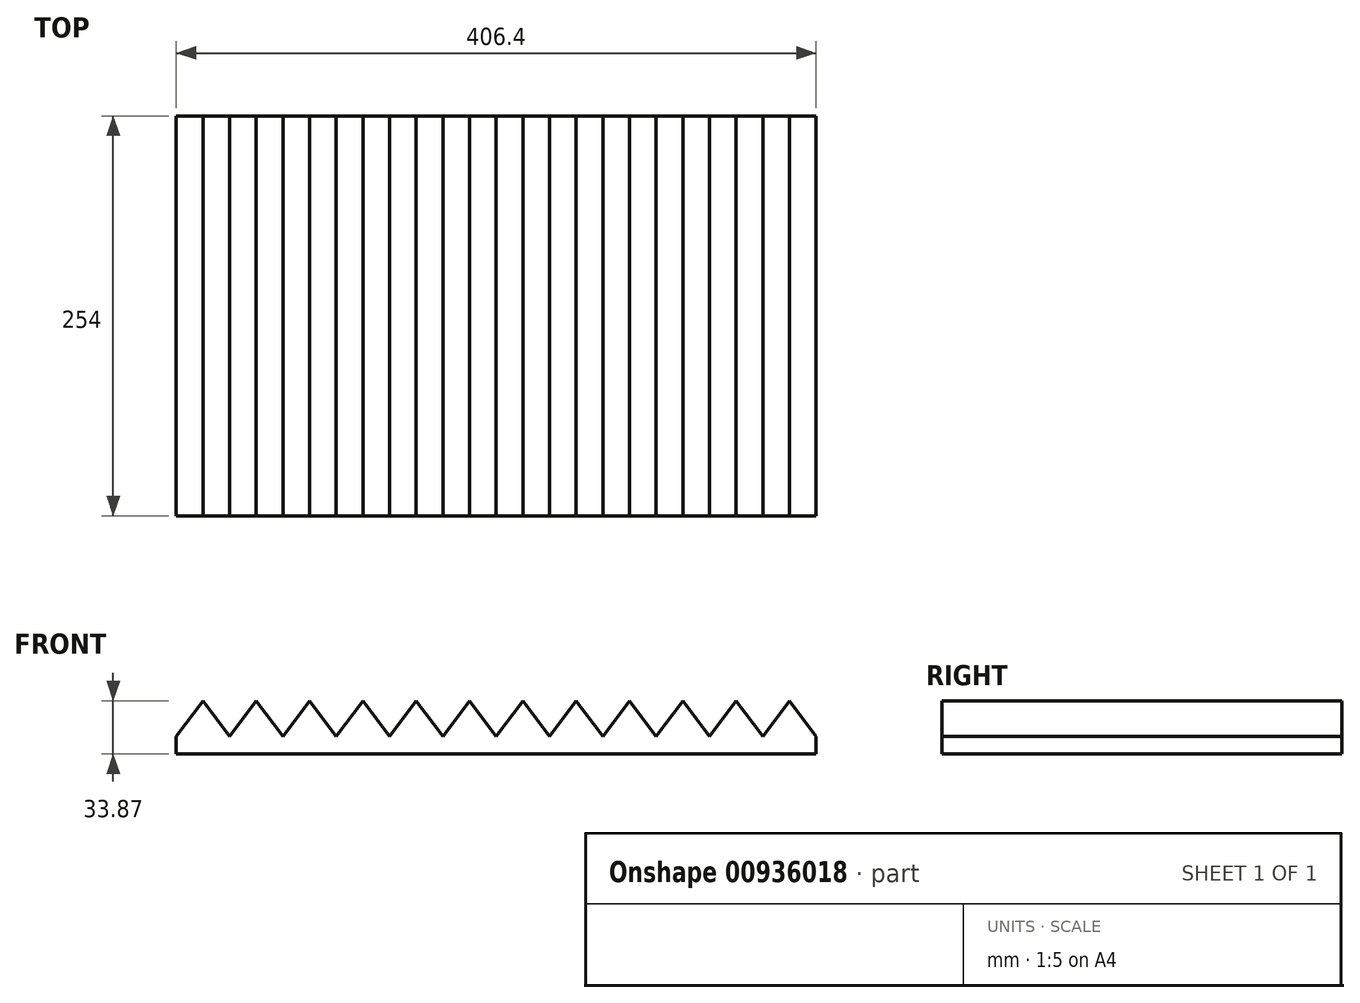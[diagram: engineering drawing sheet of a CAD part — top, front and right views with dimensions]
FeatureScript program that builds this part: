
annotation { "Feature Type Name" : "Feature", "Feature Type Description" : "" }
export const myFeature = defineFeature(function(context is Context, id is Id, definition is map)
    precondition{}
    {
        {
            var Q0;
            Q0=qCreatedBy(makeId("Front.planeOp"),FACE);
            var sketch = newSketch(context, id + "F0", { "sketchPlane" : qUnion([Q0])});
            skLineSegment(sketch, "E0.bottom", {"start": v(-198.97, -4.94) * mm, "end": v(207.43, -4.94) * mm});
            skLineSegment(sketch, "E0.top", {"start": v(-198.97, 6.35) * mm, "end": v(207.43, 6.35) * mm});
            skLineSegment(sketch, "E0.left", {"start": v(-198.97, -4.94) * mm, "end": v(-198.97, 6.35) * mm});
            skLineSegment(sketch, "E0.right", {"start": v(207.43, -4.94) * mm, "end": v(207.43, 6.35) * mm});
            skLineSegment(sketch, "E1", {"start": v(-198.97, 6.35) * mm, "end": v(-165.1, 6.35) * mm});
            skPoint(sketch, "E2", {"position": v(-198.97, 6.35) * mm});
            skLineSegment(sketch, "E3", {"start": v(-165.1, 6.35) * mm, "end": v(-198.97, 6.35) * mm});
            skLineSegment(sketch, "E4", {"start": v(-182.03, 6.35) * mm, "end": v(-182.03, 28.93) * mm});
            skLineSegment(sketch, "E5", {"start": v(-165.1, 6.35) * mm, "end": v(-182.03, 28.93) * mm});
            skLineSegment(sketch, "E6", {"start": v(-198.97, 6.35) * mm, "end": v(-182.03, 28.93) * mm});
            skLineSegment(sketch, "E7.direction1", {"start": v(-198.97, 6.35) * mm, "end": v(-129.54, 6.35) * mm, "construction": true});
            skLineSegment(sketch, "E8.1.0.0", {"start": v(-165.1, 6.35) * mm, "end": v(-148.17, 28.93) * mm});
            skLineSegment(sketch, "E8.1.0.1", {"start": v(-148.17, 6.35) * mm, "end": v(-148.17, 28.93) * mm});
            skLineSegment(sketch, "E8.1.0.2", {"start": v(-131.23, 6.35) * mm, "end": v(-148.17, 28.93) * mm});
            skLineSegment(sketch, "E8.2.0.0", {"start": v(-131.23, 6.35) * mm, "end": v(-114.3, 28.93) * mm});
            skLineSegment(sketch, "E8.2.0.1", {"start": v(-114.3, 6.35) * mm, "end": v(-114.3, 28.93) * mm});
            skLineSegment(sketch, "E8.2.0.2", {"start": v(-97.37, 6.35) * mm, "end": v(-114.3, 28.93) * mm});
            skLineSegment(sketch, "E8.3.0.0", {"start": v(-97.37, 6.35) * mm, "end": v(-80.43, 28.93) * mm});
            skLineSegment(sketch, "E8.3.0.1", {"start": v(-80.43, 6.35) * mm, "end": v(-80.43, 28.93) * mm});
            skLineSegment(sketch, "E8.3.0.2", {"start": v(-63.5, 6.35) * mm, "end": v(-80.43, 28.93) * mm});
            skLineSegment(sketch, "E8.4.0.0", {"start": v(-63.5, 6.35) * mm, "end": v(-46.57, 28.93) * mm});
            skLineSegment(sketch, "E8.4.0.1", {"start": v(-46.57, 6.35) * mm, "end": v(-46.57, 28.93) * mm});
            skLineSegment(sketch, "E8.4.0.2", {"start": v(-29.63, 6.35) * mm, "end": v(-46.57, 28.93) * mm});
            skLineSegment(sketch, "E8.5.0.0", {"start": v(-29.63, 6.35) * mm, "end": v(-12.7, 28.93) * mm});
            skLineSegment(sketch, "E8.5.0.1", {"start": v(-12.7, 6.35) * mm, "end": v(-12.7, 28.93) * mm});
            skLineSegment(sketch, "E8.5.0.2", {"start": v(4.23, 6.35) * mm, "end": v(-12.7, 28.93) * mm});
            skLineSegment(sketch, "E8.6.0.0", {"start": v(4.23, 6.35) * mm, "end": v(21.17, 28.93) * mm});
            skLineSegment(sketch, "E8.6.0.1", {"start": v(21.17, 6.35) * mm, "end": v(21.17, 28.93) * mm});
            skLineSegment(sketch, "E8.6.0.2", {"start": v(38.1, 6.35) * mm, "end": v(21.17, 28.93) * mm});
            skLineSegment(sketch, "E8.7.0.0", {"start": v(38.1, 6.35) * mm, "end": v(55.03, 28.93) * mm});
            skLineSegment(sketch, "E8.7.0.1", {"start": v(55.03, 6.35) * mm, "end": v(55.03, 28.93) * mm});
            skLineSegment(sketch, "E8.7.0.2", {"start": v(71.97, 6.35) * mm, "end": v(55.03, 28.93) * mm});
            skLineSegment(sketch, "E8.8.0.0", {"start": v(71.97, 6.35) * mm, "end": v(88.9, 28.93) * mm});
            skLineSegment(sketch, "E8.8.0.1", {"start": v(88.9, 6.35) * mm, "end": v(88.9, 28.93) * mm});
            skLineSegment(sketch, "E8.8.0.2", {"start": v(105.83, 6.35) * mm, "end": v(88.9, 28.93) * mm});
            skLineSegment(sketch, "E8.9.0.0", {"start": v(105.83, 6.35) * mm, "end": v(122.77, 28.93) * mm});
            skLineSegment(sketch, "E8.9.0.1", {"start": v(122.77, 6.35) * mm, "end": v(122.77, 28.93) * mm});
            skLineSegment(sketch, "E8.9.0.2", {"start": v(139.7, 6.35) * mm, "end": v(122.77, 28.93) * mm});
            skLineSegment(sketch, "E8.10.0.0", {"start": v(139.7, 6.35) * mm, "end": v(156.63, 28.93) * mm});
            skLineSegment(sketch, "E8.10.0.1", {"start": v(156.63, 6.35) * mm, "end": v(156.63, 28.93) * mm});
            skLineSegment(sketch, "E8.10.0.2", {"start": v(173.57, 6.35) * mm, "end": v(156.63, 28.93) * mm});
            skLineSegment(sketch, "E8.11.0.0", {"start": v(173.57, 6.35) * mm, "end": v(190.5, 28.93) * mm});
            skLineSegment(sketch, "E8.11.0.1", {"start": v(190.5, 6.35) * mm, "end": v(190.5, 28.93) * mm});
            skLineSegment(sketch, "E8.11.0.2", {"start": v(207.43, 6.35) * mm, "end": v(190.5, 28.93) * mm});
            skLineSegment(sketch, "E8.direction1", {"start": v(-198.97, 6.35) * mm, "end": v(-165.1, 6.35) * mm, "construction": true});
            skSolve(sketch);
        }
        {
            var Q0;
            Q0 = qSketchRegion(id + "F0", true);
            extrude(context, id + "F1", {"entities" : qUnion([Q0]), "depth" : 254 * mm, "offsetDistance" : 25 * mm});
        }
    });
